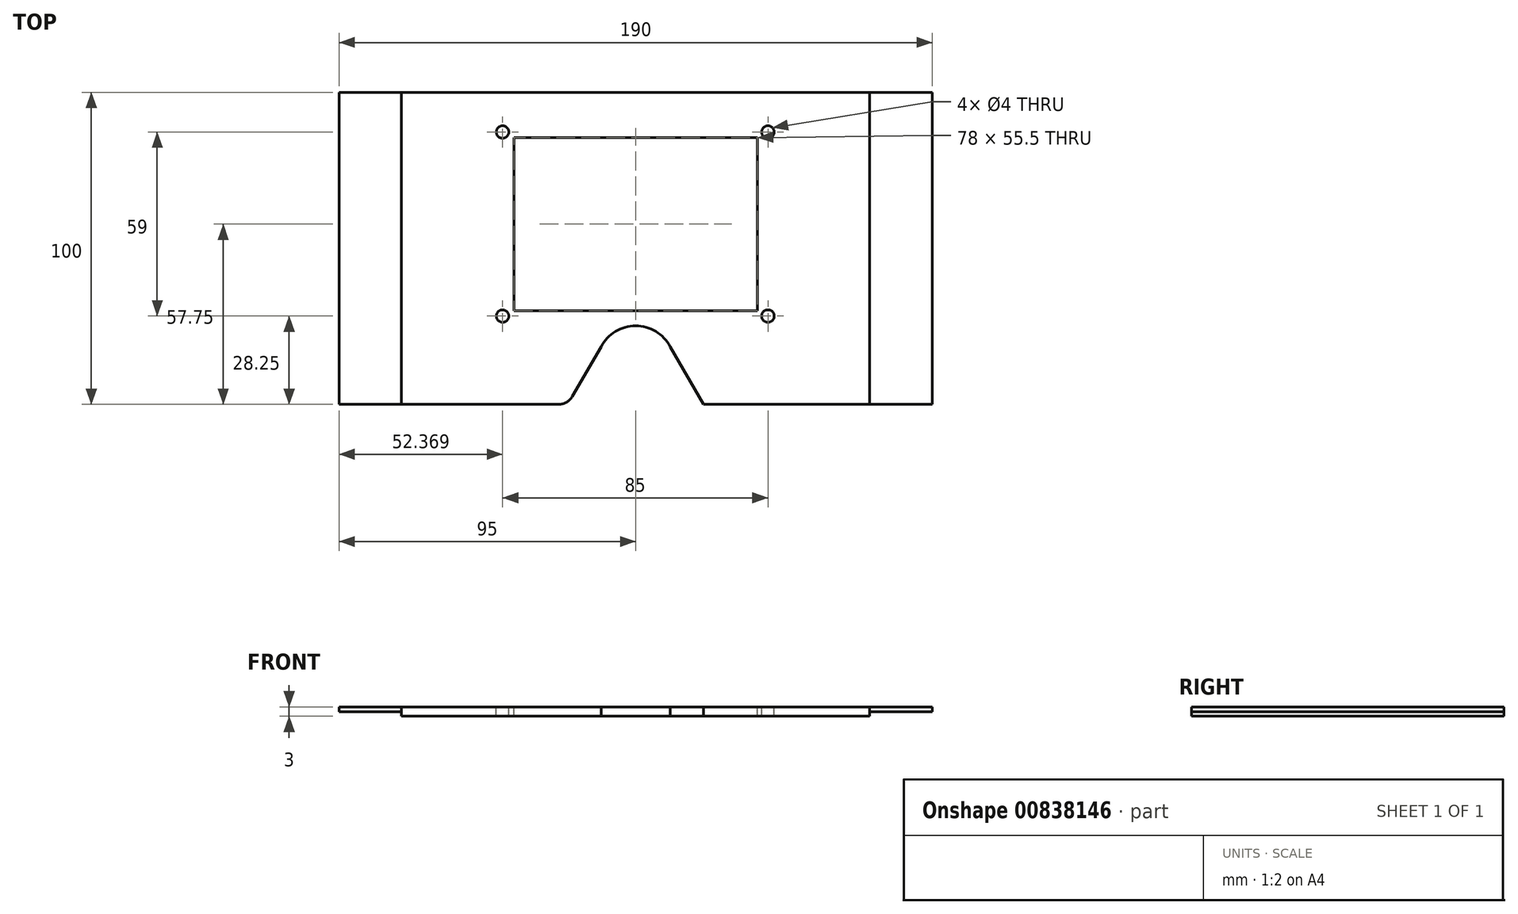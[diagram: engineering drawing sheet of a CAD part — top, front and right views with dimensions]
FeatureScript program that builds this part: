
annotation { "Feature Type Name" : "Feature", "Feature Type Description" : "" }
export const myFeature = defineFeature(function(context is Context, id is Id, definition is map)
    precondition{}
    {
        {
            var Q0;
            Q0=qCreatedBy(makeId("Top.planeOp"),FACE);
            var sketch = newSketch(context, id + "F0", { "sketchPlane" : qUnion([Q0])});
            skLineSegment(sketch, "E0", {"start": v(-202.23, 0) * mm, "end": v(-197.81, 20.8) * mm});
            skLineSegment(sketch, "E1", {"start": v(216.1, 0) * mm, "end": v(-202.23, 0) * mm});
            skLineSegment(sketch, "E2", {"start": v(-100, 100) * mm, "end": v(100, 100) * mm});
            skArc(sketch, "E3", {"start": v(-100, 100) * mm, "mid": v(-162.93, 77.71) * mm, "end": v(-197.81, 20.8) * mm});
            skArc(sketch, "E4", {"start": v(209.29, 20.8) * mm, "mid": v(167.49, 78.12) * mm, "end": v(100, 100) * mm});
            skLineSegment(sketch, "E5", {"start": v(0, 100) * mm, "end": v(0, 0) * mm, "construction": true});
            skLineSegment(sketch, "E6", {"start": v(216.1, 0) * mm, "end": v(209.29, 20.8) * mm});
            skSolve(sketch);
        }
        {
            var Q0;
            Q0=qSketchRegion(id+"F0",true);
            extrude(context, id + "F1", {"entities" : qUnion([Q0]), "depth" : 3 * mm, "offsetDistance" : 25 * mm});
        }
        {
            var Q0;
            Q0=makeQuery(id+"F1.opExtrude","CAP_FACE",FACE,{"disambiguationData":[OSD([sQuery(id+"F0.wireOp",EDGE,"E0"),sQuery(id+"F0.wireOp",EDGE,"E1"),sQuery(id+"F0.wireOp",EDGE,"E2"),sQuery(id+"F0.wireOp",EDGE,"E3"),sQuery(id+"F0.wireOp",EDGE,"E4"),sQuery(id+"F0.wireOp",EDGE,"E6")])],"isStart":false});
            var sketch = newSketch(context, id + "F2", { "sketchPlane" : qUnion([Q0])});
            skCircle(sketch, "E7", {"center": v(0, 12.5) * mm, "radius": 12.6 * mm});
            skLineSegment(sketch, "E8", {"start": v(-11.1, 18.46) * mm, "end": v(-21.76, 0) * mm});
            skLineSegment(sketch, "E9", {"start": v(11.1, 18.46) * mm, "end": v(21.76, 0) * mm});
            skLineSegment(sketch, "E10", {"start": v(21.76, 0) * mm, "end": v(-21.76, 0) * mm});
            skSolve(sketch);
        }
        {
            var Q0;
            Q0=qSketchRegion(id+"F2",true);
            extrude(context, id + "F3", {"entities" : qUnion([Q0]), "operationType" : NewBodyOperationType.REMOVE, "oppositeDirection" : true, "depth" : 25 * mm, "offsetDistance" : 25 * mm});
        }
        {
            var Q0;
            Q0=makeQuery(id+"F3.boolean.opBoolean","COPY",EDGE,{"derivedFrom":makeQuery(id+"F3.opExtrude","SWEPT_EDGE",EDGE,{"disambiguationData":[OSD([sQuery(id+"F0.wireOp",EDGE,"E1"),sQuery(id+"F2.wireOp",EDGE,"E8"),sQuery(id+"F2.wireOp",EDGE,"E10")])]})});
            var Q1;
            Q1=makeQuery(id+"F3.boolean.opBoolean","COPY",EDGE,{"derivedFrom":makeQuery(id+"F3.opExtrude","SWEPT_EDGE",EDGE,{"disambiguationData":[OSD([sQuery(id+"F0.wireOp",EDGE,"E1"),sQuery(id+"F2.wireOp",EDGE,"E9"),sQuery(id+"F2.wireOp",EDGE,"E10")])]})});
            fillet(context, id + "F4", {"entities" : qUnion([Q0, Q1]), "radius" : 5 * mm, "tangentPropagation" : true, "allowEdgeOverflow" : false});
        }
        {
            var Q0;
            Q0=makeQuery(id+"F1.opExtrude","CAP_FACE",FACE,{"disambiguationData":[OSD([sQuery(id+"F0.wireOp",EDGE,"E0"),sQuery(id+"F0.wireOp",EDGE,"E1"),sQuery(id+"F0.wireOp",EDGE,"E2"),sQuery(id+"F0.wireOp",EDGE,"E3"),sQuery(id+"F0.wireOp",EDGE,"E4"),sQuery(id+"F0.wireOp",EDGE,"E6")])],"isStart":false});
            var sketch = newSketch(context, id + "F5", { "sketchPlane" : qUnion([Q0])});
            skCircle(sketch, "E11.cCircle", {"center": v(-145, 30) * mm, "radius": 8.95 * mm, "construction": true});
            skLineSegment(sketch, "E11.0", {"start": v(-152.75, 34.47) * mm, "end": v(-145, 38.95) * mm});
            skLineSegment(sketch, "E11.1", {"start": v(-145, 38.95) * mm, "end": v(-137.25, 34.47) * mm});
            skLineSegment(sketch, "E11.2", {"start": v(-137.25, 34.47) * mm, "end": v(-137.25, 25.53) * mm});
            skLineSegment(sketch, "E11.3", {"start": v(-137.25, 25.53) * mm, "end": v(-145, 21.05) * mm});
            skLineSegment(sketch, "E11.4", {"start": v(-145, 21.05) * mm, "end": v(-152.75, 25.53) * mm});
            skLineSegment(sketch, "E11.5", {"start": v(-152.75, 25.53) * mm, "end": v(-152.75, 34.47) * mm});
            skCircle(sketch, "E12", {"center": v(-115, 30) * mm, "radius": 11.15 * mm});
            skCircle(sketch, "E13", {"center": v(-115, 60) * mm, "radius": 2.65 * mm});
            skCircle(sketch, "E14", {"center": v(-145, 60) * mm, "radius": 2.65 * mm});
            skSolve(sketch);
        }
        {
            var Q0;
            Q0=qSketchRegion(id+"F5",true);
            extrude(context, id + "F6", {"entities" : qUnion([Q0]), "operationType" : NewBodyOperationType.REMOVE, "oppositeDirection" : true, "depth" : 25 * mm, "offsetDistance" : 25 * mm});
        }
        {
            var Q0;
            Q0=makeQuery(id+"F1.opExtrude","CAP_FACE",FACE,{"disambiguationData":[OSD([sQuery(id+"F0.wireOp",EDGE,"E0"),sQuery(id+"F0.wireOp",EDGE,"E1"),sQuery(id+"F0.wireOp",EDGE,"E2"),sQuery(id+"F0.wireOp",EDGE,"E3"),sQuery(id+"F0.wireOp",EDGE,"E4"),sQuery(id+"F0.wireOp",EDGE,"E6")])],"isStart":false});
            var sketch = newSketch(context, id + "F7", { "sketchPlane" : qUnion([Q0])});
            skLineSegment(sketch, "E15.bottom", {"start": v(-39, 30) * mm, "end": v(39, 30) * mm});
            skLineSegment(sketch, "E15.top", {"start": v(-39, 85.5) * mm, "end": v(39, 85.5) * mm});
            skLineSegment(sketch, "E15.left", {"start": v(-39, 30) * mm, "end": v(-39, 85.5) * mm});
            skLineSegment(sketch, "E15.right", {"start": v(39, 30) * mm, "end": v(39, 85.5) * mm});
            skCircle(sketch, "E16", {"center": v(-42.63, 28.25) * mm, "radius": 2 * mm});
            skCircle(sketch, "E17", {"center": v(-42.63, 87.25) * mm, "radius": 2 * mm});
            skCircle(sketch, "E18", {"center": v(42.37, 87.25) * mm, "radius": 2 * mm});
            skCircle(sketch, "E19", {"center": v(42.37, 28.25) * mm, "radius": 2 * mm});
            skLineSegment(sketch, "E20", {"start": v(0, 85.5) * mm, "end": v(0, 30) * mm, "construction": true});
            skSolve(sketch);
        }
        {
            var Q0;
            Q0=qSketchRegion(id+"F7",true);
            extrude(context, id + "F8", {"entities" : qUnion([Q0]), "operationType" : NewBodyOperationType.REMOVE, "oppositeDirection" : true, "depth" : 25 * mm, "offsetDistance" : 25 * mm});
        }
        {
            var Q0;
            Q0=makeQuery(id+"F1.opExtrude","CAP_FACE",FACE,{"disambiguationData":[OSD([sQuery(id+"F0.wireOp",EDGE,"E0"),sQuery(id+"F0.wireOp",EDGE,"E1"),sQuery(id+"F0.wireOp",EDGE,"E2"),sQuery(id+"F0.wireOp",EDGE,"E3"),sQuery(id+"F0.wireOp",EDGE,"E4"),sQuery(id+"F0.wireOp",EDGE,"E6")])],"isStart":false});
            var sketch = newSketch(context, id + "F9", { "sketchPlane" : qUnion([Q0])});
            skCircle(sketch, "E21", {"center": v(115, 30) * mm, "radius": 8.15 * mm});
            skSolve(sketch);
        }
        {
            var Q0;
            Q0=qSketchRegion(id+"F9",true);
            extrude(context, id + "F10", {"entities" : qUnion([Q0]), "operationType" : NewBodyOperationType.REMOVE, "oppositeDirection" : true, "depth" : 25 * mm, "offsetDistance" : 25 * mm});
        }
        {
            var Q0;
            Q0=makeQuery(id+"F1.opExtrude","CAP_FACE",FACE,{"disambiguationData":[OSD([sQuery(id+"F0.wireOp",EDGE,"E0"),sQuery(id+"F0.wireOp",EDGE,"E1"),sQuery(id+"F0.wireOp",EDGE,"E2"),sQuery(id+"F0.wireOp",EDGE,"E3"),sQuery(id+"F0.wireOp",EDGE,"E4"),sQuery(id+"F0.wireOp",EDGE,"E6")])],"isStart":false});
            var sketch = newSketch(context, id + "F11", { "sketchPlane" : qUnion([Q0])});
            skArc(sketch, "E22", {"start": v(-100, 95) * mm, "mid": v(-155.57, 77.06) * mm, "end": v(-190.14, 30) * mm});
            skPoint(sketch, "E22.endSnap0", {"position": v(-152.75, 30) * mm});
            skLineSegment(sketch, "E23", {"start": v(-100, 95) * mm, "end": v(100, 95) * mm});
            skArc(sketch, "E24", {"start": v(200.37, 30) * mm, "mid": v(159.8, 77.33) * mm, "end": v(100, 95) * mm});
            skSolve(sketch);
        }
        {
            var Q0;
            {var subQ5=sQuery(id+"F0.wireOp",EDGE,"E0");Q0=makeQuery(id+"F11.imprint","IMPRINT",FACE,{"disambiguationData":[TD([[makeQuery(id+"F11.imprint","IMPRINT",EDGE,{"derivedFrom":makeQuery(id+"F1.opExtrude","CAP_EDGE",EDGE,{"disambiguationData":[OSD([subQ5])],"isStart":false})}),-1.0]])]});}
            var sketch = newSketch(context, id + "F12", { "sketchPlane" : qUnion([Q0])});
            skLineSegment(sketch, "E25.bottom", {"start": v(-75, 0) * mm, "end": v(-213.95, 0) * mm});
            skLineSegment(sketch, "E25.top", {"start": v(-75, 109.39) * mm, "end": v(-213.95, 109.39) * mm});
            skLineSegment(sketch, "E25.left", {"start": v(-75, 0) * mm, "end": v(-75, 109.39) * mm});
            skLineSegment(sketch, "E25.right", {"start": v(-213.95, 0) * mm, "end": v(-213.95, 109.39) * mm});
            skLineSegment(sketch, "E26.bottom", {"start": v(75, 0) * mm, "end": v(225.4, 0) * mm});
            skLineSegment(sketch, "E26.top", {"start": v(75, 110.1) * mm, "end": v(225.4, 110.1) * mm});
            skLineSegment(sketch, "E26.left", {"start": v(75, 0) * mm, "end": v(75, 110.1) * mm});
            skLineSegment(sketch, "E26.right", {"start": v(225.4, 0) * mm, "end": v(225.4, 110.1) * mm});
            skSolve(sketch);
        }
        {
            var Q0;
            Q0 = qSketchRegion(id + "F12", true);
            extrude(context, id + "F13", {"entities" : qUnion([Q0]), "operationType" : NewBodyOperationType.REMOVE, "oppositeDirection" : true, "depth" : 25 * mm, "offsetDistance" : 25 * mm});
        }
        {
            var Q0;
            {var subQ5=sQuery(id+"F0.wireOp",EDGE,"E0");Q0=makeQuery(id+"F11.imprint","IMPRINT",FACE,{"disambiguationData":[TD([[makeQuery(id+"F11.imprint","IMPRINT",EDGE,{"derivedFrom":makeQuery(id+"F1.opExtrude","CAP_EDGE",EDGE,{"disambiguationData":[OSD([subQ5])],"isStart":false})}),-1.0]])]});}
            var sketch = newSketch(context, id + "F14", { "sketchPlane" : qUnion([Q0])});
            skLineSegment(sketch, "E27.bottom", {"start": v(-75, 0) * mm, "end": v(-95, 0) * mm});
            skLineSegment(sketch, "E27.top", {"start": v(-75, 100) * mm, "end": v(-95, 100) * mm});
            skLineSegment(sketch, "E27.left", {"start": v(-75, 0) * mm, "end": v(-75, 100) * mm});
            skLineSegment(sketch, "E27.right", {"start": v(-95, 0) * mm, "end": v(-95, 100) * mm});
            skLineSegment(sketch, "E28.MirrorCS", {"start": v(75, 0) * mm, "end": v(75, 100) * mm});
            skLineSegment(sketch, "E29.MirrorCS", {"start": v(75, 100) * mm, "end": v(95, 100) * mm});
            skLineSegment(sketch, "E30.MirrorCS", {"start": v(95, 0) * mm, "end": v(95, 100) * mm});
            skLineSegment(sketch, "E31.MirrorCS", {"start": v(75, 0) * mm, "end": v(95, 0) * mm});
            skSolve(sketch);
        }
        {
            var Q0;
            Q0 = qSketchRegion(id + "F14", true);
            extrude(context, id + "F15", {"entities" : qUnion([Q0]), "oppositeDirection" : true, "depth" : 1.5 * mm, "offsetDistance" : 25 * mm});
        }
    });
